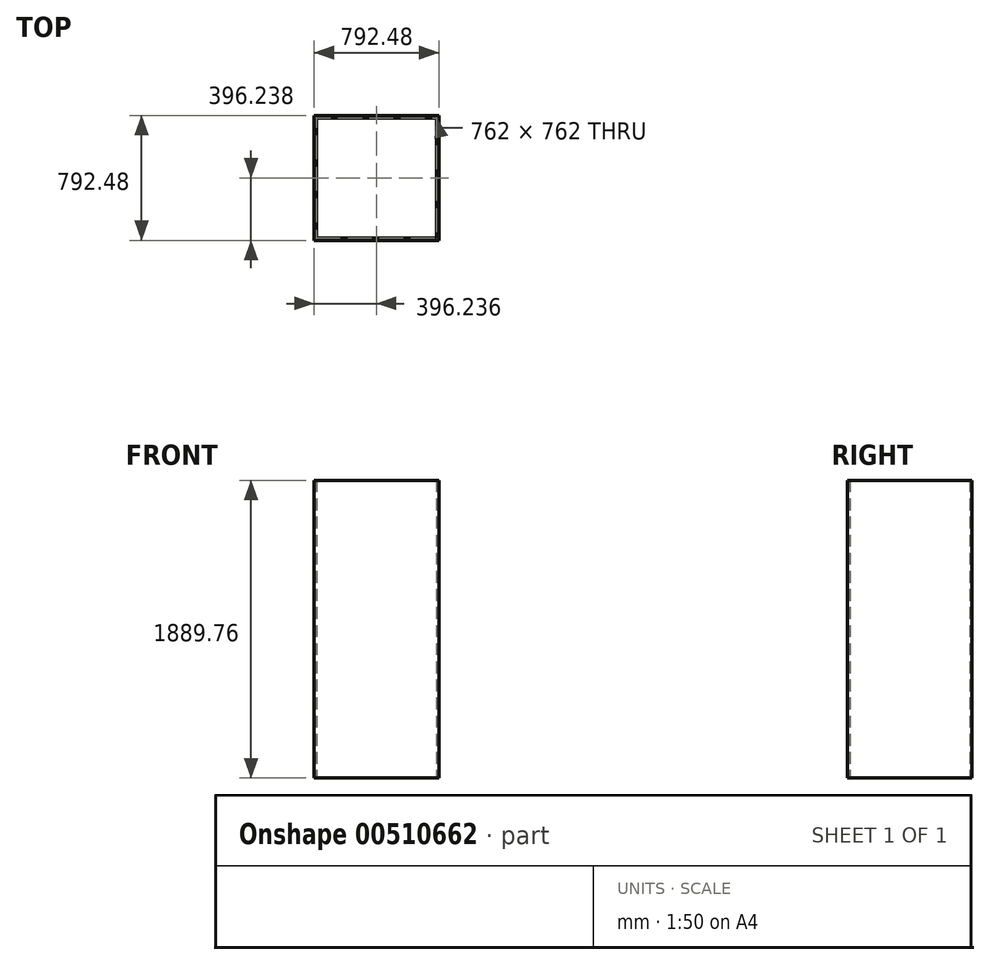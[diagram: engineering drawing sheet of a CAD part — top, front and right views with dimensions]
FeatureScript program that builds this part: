
annotation { "Feature Type Name" : "Feature", "Feature Type Description" : "" }
export const myFeature = defineFeature(function(context is Context, id is Id, definition is map)
    precondition{}
    {
        {
            var Q0;
            Q0=qCreatedBy(makeId("Top.planeOp"),FACE);
            var sketch = newSketch(context, id + "F0", { "sketchPlane" : qUnion([Q0])});
            skLineSegment(sketch, "E0.bottom", {"start": v(-372.33, 360.7) * mm, "end": v(389.67, 360.7) * mm});
            skLineSegment(sketch, "E0.top", {"start": v(-372.33, -401.3) * mm, "end": v(389.67, -401.3) * mm});
            skLineSegment(sketch, "E0.left", {"start": v(-372.33, 360.7) * mm, "end": v(-372.33, -401.3) * mm});
            skLineSegment(sketch, "E0.right", {"start": v(389.67, 360.7) * mm, "end": v(389.67, -401.3) * mm});
            skLineSegment(sketch, "E1.bottom", {"start": v(-387.57, 375.95) * mm, "end": v(404.9, 375.95) * mm});
            skLineSegment(sketch, "E1.top", {"start": v(-387.57, -416.53) * mm, "end": v(404.9, -416.53) * mm});
            skLineSegment(sketch, "E1.left", {"start": v(-387.57, 375.95) * mm, "end": v(-387.57, -416.53) * mm});
            skLineSegment(sketch, "E1.right", {"start": v(404.9, 375.95) * mm, "end": v(404.9, -416.53) * mm});
            skSolve(sketch);
        }
        {
            var Q0;
            Q0 = qSketchRegion(id + "F0", true);
            extrude(context, id + "F1", {"entities" : qUnion([Q0]), "depth" : 1889.76 * mm, "offsetDistance" : 30.48 * mm});
        }
    });
